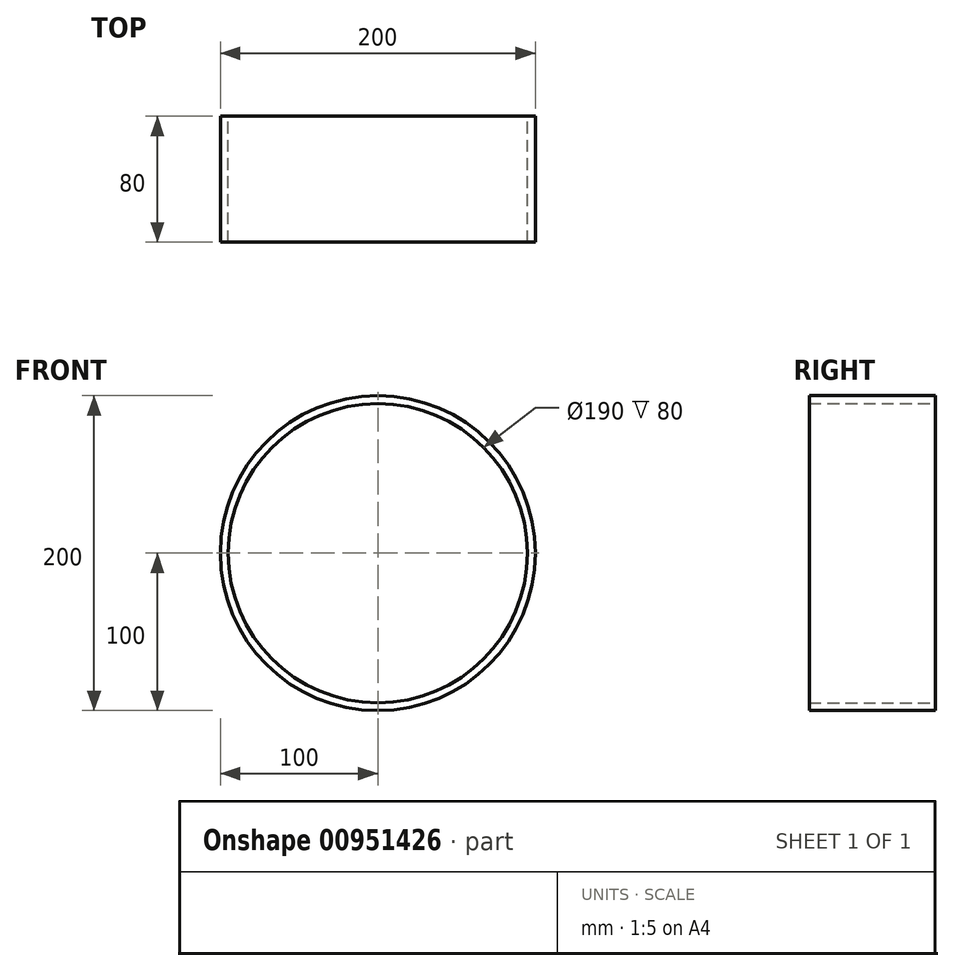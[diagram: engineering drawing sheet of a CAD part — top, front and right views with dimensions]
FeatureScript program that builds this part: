
annotation { "Feature Type Name" : "Feature", "Feature Type Description" : "" }
export const myFeature = defineFeature(function(context is Context, id is Id, definition is map)
    precondition{}
    {
        {
            var Q0;
            Q0=qCreatedBy(makeId("Front.planeOp"),FACE);
            var sketch = newSketch(context, id + "F0", { "sketchPlane" : qUnion([Q0])});
            skCircle(sketch, "E0", {"center": v(0, 0) * mm, "radius": 100 * mm});
            skCircle(sketch, "E1", {"center": v(0, 0) * mm, "radius": 95 * mm});
            skSolve(sketch);
        }
        {
            var Q0;
            Q0 = qSketchRegion(id + "F0", true);
            extrude(context, id + "F1", {"entities" : qUnion([Q0]), "depth" : 80 * mm, "offsetDistance" : 25 * mm});
        }
    });
